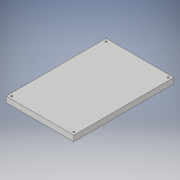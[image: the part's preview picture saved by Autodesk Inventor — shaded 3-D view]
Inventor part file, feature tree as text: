
AUTODESK INVENTOR PART (.ipt)
format: ipt  version: 2019 (Build 230136000, 136)  size: 111,616 bytes
history: native  units: in
note: dims shown in document units (in); Inventor stores cm internally (conversion verified against a paired STEP export)
features: thread x4, sketch x2, extrude x1, hole x1
ambient origin geometry x8: Origin, YZ Plane, XZ Plane, XY Plane, X Axis, Y Axis, Z Axis, Center Point
bodies: Solid1 (feature_tree)
feature tree (8):
  extrude  "Extrusion1"  Depth=4.7441in
  hole  "Hole1"  [1 undecoded]
  thread  "Thread1"  [1 undecoded]
  thread  "Thread2"  [1 undecoded]
  thread  "Thread3"  [1 undecoded]
  thread  "Thread4"  [1 undecoded]
  sketch  "Sketch1"  dims[d1=7.0079in d2=4.7441in]
  sketch  "Sketch2"  dims[d3=0.3937in d4=0.0in d5=0.1181in d6=0.1969in d7=0.1969in d8=3.5039in d9=2.372in d10=0.1181in d11=0.2953in d12=0.1476in d13=0.0984in d14=90.0deg d15=0.7874in d16=0.8108in d17=0.3937in d18=0.0in d19=0.3937in d20=0.0in d21=0.3937in d22=0.0in d23=0.3937in d24=0.0in]
note: 5 required parameter values undecoded (feature->parameter linkage not recoverable at this tier; creation-order binding heuristic only, values carry confidence <= 0.55)
